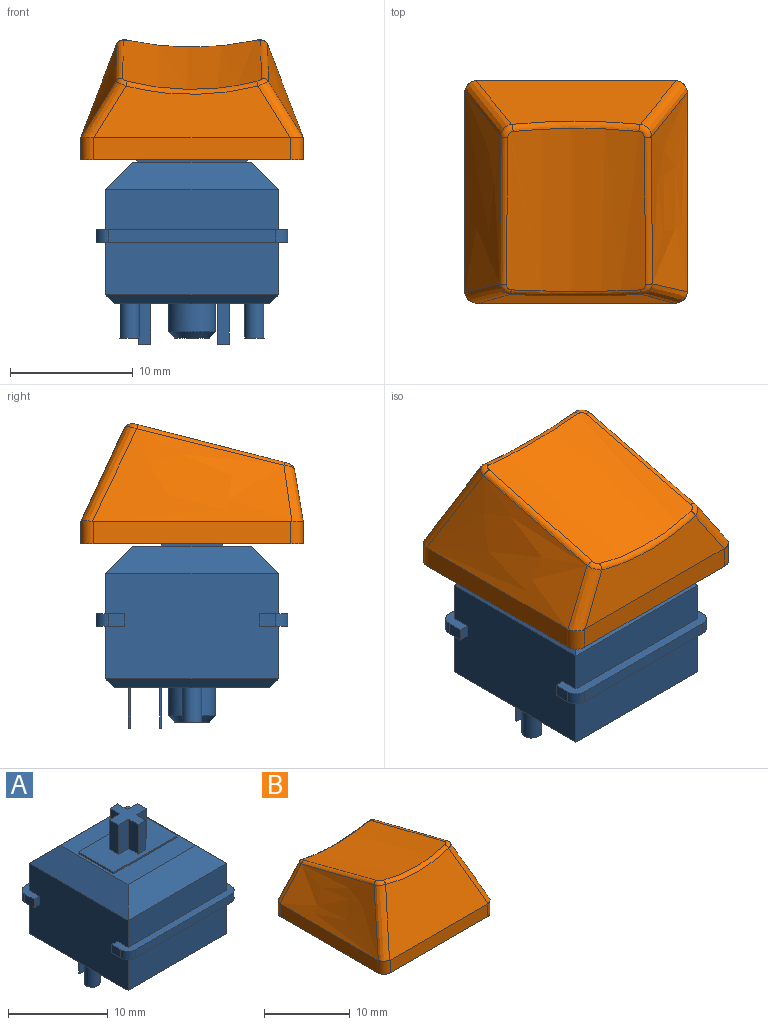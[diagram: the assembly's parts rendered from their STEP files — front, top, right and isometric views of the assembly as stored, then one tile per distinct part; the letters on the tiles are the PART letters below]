
ASSEMBLY  parts=2 mates=1
PART A: 69 faces, bbox 15.6x15.6x18.6 mm
  f0: plane 15.6x2.3mm, normal (0,0,-1), area 14.4mm2, adj f2,f3,f28,f30,f35,f60,f62,f63
  f1: plane 15.6x2.3mm, normal (0,0,-1), area 14.4mm2, adj f28,f30,f33,f34,f36,f59,f61,f64
  f2: plane 1.3x1mm, normal (1,0,0), area 1.3mm2, adj f0,f32,f62,f66
  f3: plane 1.3x1mm, normal (-1,0,0), area 1.3mm2, adj f0,f32,f63,f68
  f4: plane 15.6x2.3mm, normal (0,0,1), area 14.4mm2, adj f28,f30,f31,f33,f34,f36,f61,f64
  f5: plane 14x2.2mm, normal (-0.71,0,0.71), area 36.7mm2, adj f6,f7,f26,f30
  f6: plane 14x2.2mm, normal (0,-0.71,0.71), area 36.7mm2, adj f5,f7,f27,f31
  f7: plane 9.6x9.6mm, normal (0,0,1), area 47.2mm2, adj f5,f6,f8,f9,f10,f11,f26,f27
  f8: plane 5x0.2mm, normal (1,0,0), area 1mm2, adj f7,f9,f11,f12
  f9: plane 9x0.2mm, normal (0,1,0), area 1.8mm2, adj f7,f8,f10,f12
  f10: plane 5x0.2mm, normal (-1,0,0), area 1mm2, adj f7,f9,f11,f12
  f11: plane 9x0.2mm, normal (0,-1,0), area 1.8mm2, adj f7,f8,f10,f12
  f12: plane 9x5mm, normal (0,0,1), area 36.9mm2, adj f8,f9,f10,f11,f13,f14,f15,f16
  f13: plane 3.6x1.35mm, normal (1,0,0), area 4.9mm2, adj f12,f14,f24,f25
  f14: plane 3.6x1.08mm, normal (0,1,0), area 3.9mm2, adj f12,f13,f15,f25
  f15: plane 3.6x1.35mm, normal (-1,0,0), area 4.9mm2, adj f12,f14,f16,f25
  f16: plane 3.6x1.46mm, normal (0,1,0), area 5.3mm2, adj f12,f15,f17,f25
  f17: plane 3.6x1.3mm, normal (-1,0,0), area 4.7mm2, adj f12,f16,f18,f25
  f18: plane 3.6x1.46mm, normal (0,-1,0), area 5.3mm2, adj f12,f17,f19,f25
  f19: plane 3.6x1.35mm, normal (-1,0,0), area 4.9mm2, adj f12,f18,f20,f25
  f20: plane 3.6x1.08mm, normal (0,-1,0), area 3.9mm2, adj f12,f19,f21,f25
  f21: plane 3.6x1.35mm, normal (1,0,0), area 4.9mm2, adj f12,f20,f22,f25
  f22: plane 3.6x1.46mm, normal (0,-1,0), area 5.3mm2, adj f12,f21,f23,f25
  f23: plane 3.6x1.3mm, normal (1,0,0), area 4.7mm2, adj f12,f22,f24,f25
  f24: plane 3.6x1.46mm, normal (0,1,0), area 5.3mm2, adj f12,f13,f23,f25
  f25: plane 4x4mm, normal (0,0,1), area 8.1mm2, adj f13,f14,f15,f16,f17,f18,f19,f20
  f26: plane 14x2.2mm, normal (0,0.71,0.71), area 36.7mm2, adj f5,f7,f27,f29
  f27: plane 14x2.2mm, normal (0.71,0,0.71), area 36.7mm2, adj f6,f7,f26,f28
  f28: plane 14x8.6mm, normal (1,0,0), area 117.4mm2, adj f0,f1,f4,f27,f29,f31,f32,f55
  f29: plane 14x3.3mm, normal (0,1,0), area 46.2mm2, adj f26,f28,f30,f32
  f30: plane 14x8.6mm, normal (-1,0,0), area 117.4mm2, adj f0,f1,f4,f5,f29,f31,f32,f57
  f31: plane 14x3.3mm, normal (0,-1,0), area 46.2mm2, adj f4,f6,f28,f30
  f32: plane 15.6x2.3mm, normal (0,0,1), area 14.4mm2, adj f2,f3,f28,f29,f30,f35,f62,f63
  f33: plane 13.6x1mm, normal (0,-1,0), area 13.6mm2, adj f1,f4,f61,f64
  f34: plane 1.3x1mm, normal (1,0,0), area 1.3mm2, adj f1,f4,f61,f65
  f35: plane 13.6x1mm, normal (0,1,0), area 13.6mm2, adj f0,f32,f62,f63
  f36: plane 1.3x1mm, normal (-1,0,0), area 1.3mm2, adj f1,f4,f64,f67
  f37: plane 2.85x2.85mm, normal (0,0,-1), area 6.4mm2, adj f38
  f38: cone r=1.43mm half-angle=45deg, axis (0,0,1), area 7.4mm2, adj f37,f43
  f39: plane 1x0.2mm, normal (0,0,-1), area 0.2mm2, adj f44,f45,f46,f47
  f40: plane 1x0.2mm, normal (0,0,-1), area 0.2mm2, adj f48,f49,f50,f51
  f41: plane 1.6x1.6mm, normal (0,0,-1), area 2mm2, adj f52
  f42: plane 1.6x1.6mm, normal (0,0,-1), area 2mm2, adj f53
  f43: cylinder r=1.93mm len=3.85mm, axis (0,0,1), area 27.8mm2, adj f38,f54
  f44: plane 3.3x0.2mm, normal (-1,0,0), area 0.7mm2, adj f39,f45,f47,f54
  f45: plane 3.3x1mm, normal (0,1,0), area 3.3mm2, adj f39,f44,f46,f54
  f46: plane 3.3x0.2mm, normal (1,0,0), area 0.7mm2, adj f39,f45,f47,f54
  f47: plane 3.3x1mm, normal (0,-1,0), area 3.3mm2, adj f39,f44,f46,f54
  f48: plane 3.3x0.2mm, normal (-1,0,0), area 0.7mm2, adj f40,f49,f51,f54
  f49: plane 3.3x1mm, normal (0,1,0), area 3.3mm2, adj f40,f48,f50,f54
  f50: plane 3.3x0.2mm, normal (1,0,0), area 0.7mm2, adj f40,f49,f51,f54
  f51: plane 3.3x1mm, normal (0,-1,0), area 3.3mm2, adj f40,f48,f50,f54
  f52: cylinder r=0.8mm len=2.8mm, axis (0,0,1), area 14.1mm2, adj f41,f54
  f53: cylinder r=0.8mm len=2.8mm, axis (0,0,1), area 14.1mm2, adj f42,f54
  f54: plane 12.6x12.6mm, normal (0,0,-1), area 142.7mm2, adj f43,f44,f45,f46,f47,f48,f49,f50
  f55: plane 14x0.7mm, normal (0.71,0,-0.71), area 13.2mm2, adj f28,f54,f56,f58
  f56: plane 14x0.7mm, normal (0,0.71,-0.71), area 13.2mm2, adj f54,f55,f57,f60
  f57: plane 14x0.7mm, normal (-0.71,0,-0.71), area 13.2mm2, adj f30,f54,f56,f58
  f58: plane 14x0.7mm, normal (0,-0.71,-0.71), area 13.2mm2, adj f54,f55,f57,f59
  f59: plane 14x4.3mm, normal (0,-1,0), area 60.2mm2, adj f1,f28,f30,f58
  f60: plane 14x4.3mm, normal (0,1,0), area 60.2mm2, adj f0,f28,f30,f56
  f61: cylinder r=1mm len=1mm, axis (0,0,-1), area 1.6mm2, adj f1,f4,f33,f34
  f62: cylinder r=1mm len=1mm, axis (0,0,1), area 1.6mm2, adj f0,f2,f32,f35
  f63: cylinder r=1mm len=1mm, axis (0,0,-1), area 1.6mm2, adj f0,f3,f32,f35
  f64: cylinder r=1mm len=1mm, axis (0,0,1), area 1.6mm2, adj f1,f4,f33,f36
  f65: plane 1x0.8mm, normal (0,1,0), area 0.8mm2, adj f1,f4,f28,f34
  f66: plane 1x0.8mm, normal (0,-1,0), area 0.8mm2, adj f0,f2,f28,f32
  f67: plane 1x0.8mm, normal (0,1,0), area 0.8mm2, adj f1,f4,f30,f36
  f68: plane 1x0.8mm, normal (0,-1,0), area 0.8mm2, adj f0,f3,f30,f32
PART B: 50 faces, bbox 21.6x22.4x13.6 mm
  f0: plane 18.1x18.1mm, normal (0,0,-1), area 67.5mm2, adj f1,f2,f3,f4,f10,f12,f14,f16
  f1: plane 16.1x1.8mm, normal (1,0,0), area 29mm2, adj f0,f8,f10,f16
  f2: plane 16.1x1.8mm, normal (0,1,0), area 29mm2, adj f0,f5,f14,f15,f16,f17
  f3: plane 16.1x1.8mm, normal (-1,0,0), area 29mm2, adj f0,f6,f12,f14
  f4: plane 16.1x1.8mm, normal (0,-1,0), area 29mm2, adj f0,f7,f10,f12
  f5: plane 15.95x4.19mm, normal (0,0.99,0.17), area 51.8mm2, adj f2,f15,f17,f20
  f6: bspline ~18.1x8.19mm, area 96.8mm2, adj f3,f12,f13,f14,f15,f19
  f7: plane 16.28x7.63mm, normal (0,-0.91,0.42), area 108.3mm2, adj f4,f10,f11,f12,f13,f23
  f8: bspline ~18.1x8.19mm, area 96.8mm2, adj f1,f10,f11,f16,f17,f24
  f9: cylinder r=22.9mm len=13.05mm, axis (0,0.97,-0.25), area 150.3mm2, adj f18,f19,f20,f21,f22,f23,f24,f25
  f10: cylinder r=1mm len=1.87mm, axis (0,0,-1), area 2.9mm2, adj f0,f1,f4,f7,f8,f11
  f11: bspline ~10.14x5.57mm, area 13mm2, adj f7,f8,f10,f25
  f12: cylinder r=1mm len=1.87mm, axis (0,0,1), area 2.9mm2, adj f0,f3,f4,f6,f7,f13
  f13: bspline ~11.34x6.15mm, area 13mm2, adj f6,f7,f12,f21
  f14: cylinder r=1mm len=1.8mm, axis (0,0,-1), area 2.8mm2, adj f0,f2,f3,f6,f15
  f15: bspline ~7.36x5.16mm, area 7.5mm2, adj f2,f5,f6,f14,f18
  f16: cylinder r=1mm len=1.8mm, axis (0,0,1), area 2.8mm2, adj f0,f1,f2,f8,f17
  f17: bspline ~7.27x5.11mm, area 7.5mm2, adj f2,f5,f8,f16,f22
  f18: bspline ~1.12x0.97mm, area 0.6mm2, adj f9,f15,f19,f20
  f19: bspline ~18.33x4.95mm, area 8.5mm2, adj f6,f9,f18,f21
  f20: bspline ~10.76x1.07mm, area 6.2mm2, adj f5,f9,f18,f22
  f21: bspline ~1.23x1.17mm, area 0.8mm2, adj f9,f13,f19,f23
  f22: bspline ~1.1x0.93mm, area 0.6mm2, adj f9,f17,f20,f24
  f23: bspline ~10.45x0.83mm, area 7.2mm2, adj f7,f9,f21,f25
  f24: bspline ~18.29x4.94mm, area 8.5mm2, adj f8,f9,f22,f25
  f25: bspline ~1.33x1.08mm, area 0.8mm2, adj f9,f11,f23,f24
  f26: plane 16.18x1.7mm, normal (-1,0,0), area 25.3mm2, adj f0,f27,f29,f32,f33
  f27: plane 16.1x1.72mm, normal (0,-1,0), area 27.6mm2, adj f0,f26,f28,f30,f31,f33
  f28: plane 16.18x1.7mm, normal (1,0,0), area 25.3mm2, adj f0,f27,f29,f31,f32
  f29: plane 16.1x1.58mm, normal (0,1,0), area 25.4mm2, adj f0,f26,f28,f32
  f30: plane 16.43x4.41mm, normal (0,-0.99,-0.17), area 46.9mm2, adj f27,f31,f33,f34
  f31: offset ~20.1x10.19mm, area 87.9mm2, adj f27,f28,f30,f32,f34
  f32: plane 16.33x7.29mm, normal (0,0.91,-0.42), area 100.3mm2, adj f26,f28,f29,f31,f33,f34
  f33: offset ~20.1x10.19mm, area 87.9mm2, adj f26,f27,f30,f32,f34
  f34: cylinder r=23.9mm len=12.31mm, axis (0,0.97,-0.25), area 113.6mm2, adj f30,f31,f32,f33,f46
  f35: plane 6.62x1.35mm, normal (-1,0,0), area 8.7mm2, adj f36,f44,f45,f49
  f36: plane 6.7x1.51mm, normal (0,-1,0), area 10mm2, adj f35,f37,f45,f49
  f37: plane 7.03x1.3mm, normal (-1,0,0), area 8.9mm2, adj f36,f38,f45,f49
  f38: plane 7.04x1.51mm, normal (0,1,0), area 10.5mm2, adj f37,f39,f45,f49
  f39: plane 7.3x1.35mm, normal (-1,0,0), area 9.6mm2, adj f38,f40,f45,f49
  f40: plane 7.31x1mm, normal (0,1,0), area 7.3mm2, adj f39,f41,f45,f49
  f41: plane 7.3x1.35mm, normal (1,0,0), area 9.6mm2, adj f40,f42,f45,f49
  f42: plane 7.04x1.51mm, normal (0,1,0), area 10.5mm2, adj f41,f43,f45,f49
  f43: plane 7.03x1.3mm, normal (1,0,0), area 8.9mm2, adj f42,f45,f47,f49
  f44: plane 6.27x1mm, normal (0,-1,0), area 6.3mm2, adj f35,f45,f48,f49
  f45: plane 5.5x5.5mm, normal (0,0,-1), area 15.9mm2, adj f35,f36,f37,f38,f39,f40,f41,f42
  f46: cylinder r=2.75mm len=6.94mm, axis (0,0,-1), area 120mm2, adj f34,f45
  f47: plane 6.7x1.51mm, normal (0,-1,0), area 10mm2, adj f43,f45,f48,f49
  f48: plane 6.62x1.35mm, normal (1,0,0), area 8.7mm2, adj f44,f45,f47,f49
  f49: cylinder r=23.9mm len=4.02mm, axis (0,0.97,-0.25), area 8.2mm2, adj f35,f36,f37,f38,f39,f40,f41,f42
PLACE A at identity fixed
PLACE B rot(axis=(0,0,1),180deg) t=(0,0,11.7)mm
MATE fastened A.f38 <-> B.f46  axis (0,0,1) through (0,0,11.7)mm
